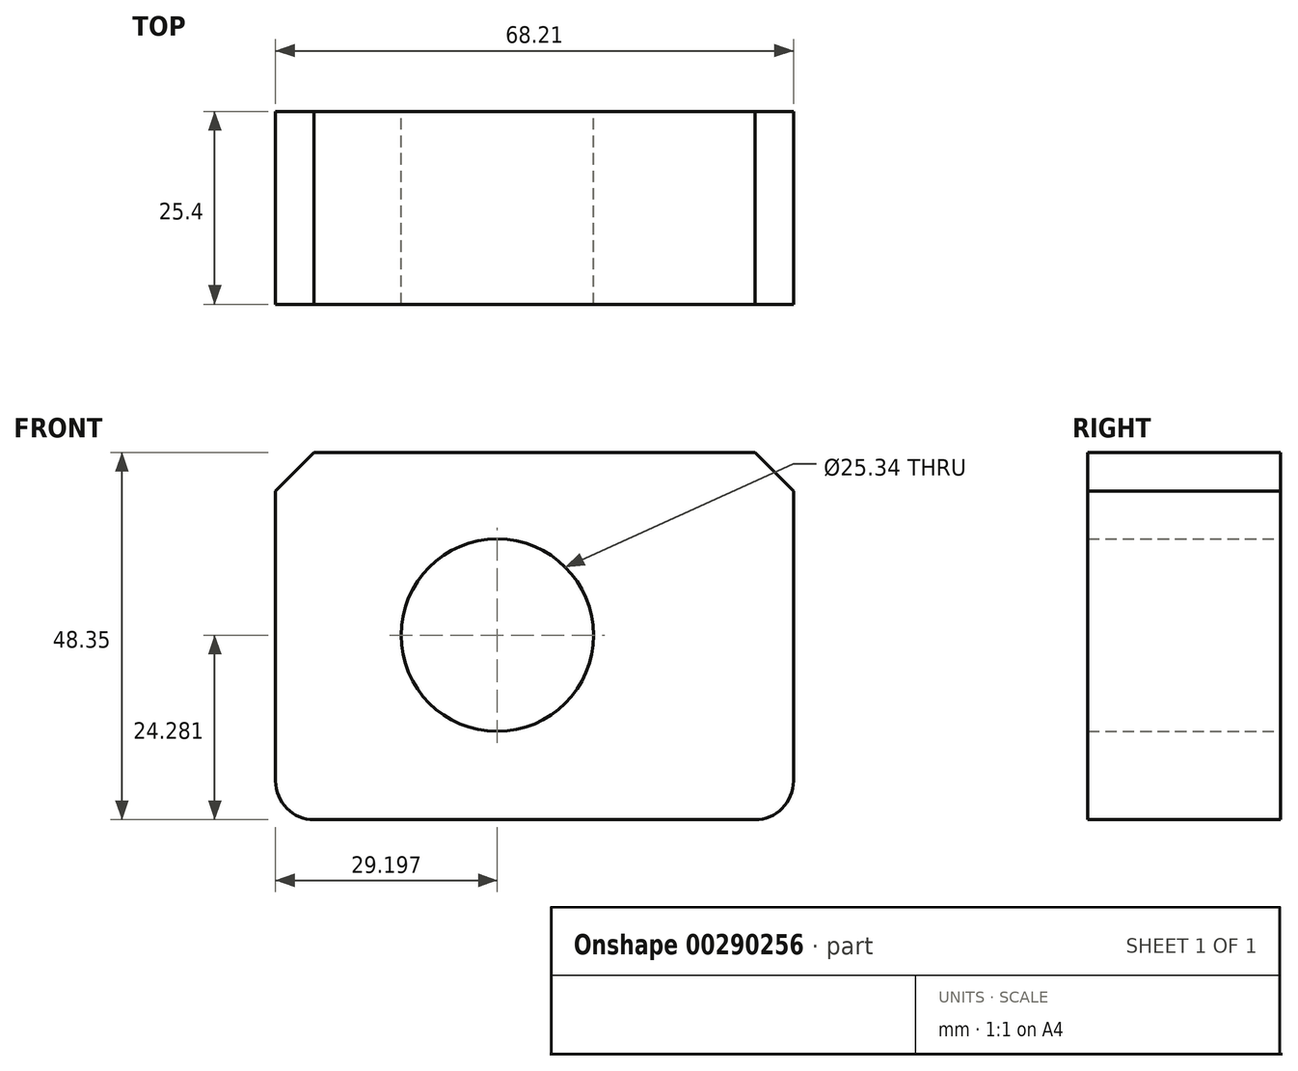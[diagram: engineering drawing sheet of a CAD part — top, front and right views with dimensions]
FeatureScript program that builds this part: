
annotation { "Feature Type Name" : "Feature", "Feature Type Description" : "" }
export const myFeature = defineFeature(function(context is Context, id is Id, definition is map)
    precondition{}
    {
        {
            var Q0;
            Q0=qCreatedBy(makeId("Front.planeOp"),FACE);
            var sketch = newSketch(context, id + "F0", { "sketchPlane" : qUnion([Q0])});
            skLineSegment(sketch, "E0.bottom", {"start": v(-45.19, 35.69) * mm, "end": v(23.02, 35.69) * mm});
            skLineSegment(sketch, "E0.top", {"start": v(-45.19, -12.66) * mm, "end": v(23.02, -12.66) * mm});
            skLineSegment(sketch, "E0.left", {"start": v(-45.19, 35.69) * mm, "end": v(-45.19, -12.66) * mm});
            skLineSegment(sketch, "E0.right", {"start": v(23.02, 35.69) * mm, "end": v(23.02, -12.66) * mm});
            skCircle(sketch, "E1", {"center": v(-16, 11.62) * mm, "radius": 12.67 * mm});
            skSolve(sketch);
        }
        {
            var Q0;
            Q0 = qSketchRegion(id + "F0", true);
            extrude(context, id + "F1", {"entities" : qUnion([Q0]), "depth" : 25.4 * mm});
        }
        {
            var Q0;
            Q0=makeQuery(id+"F1.opExtrude","SWEPT_EDGE",EDGE,{"disambiguationData":[OSD([sQuery(id+"F0.wireOp",EDGE,"E0.bottom"),sQuery(id+"F0.wireOp",EDGE,"E0.right")])]});
            var Q1;
            Q1=makeQuery(id+"F1.opExtrude","SWEPT_EDGE",EDGE,{"disambiguationData":[OSD([sQuery(id+"F0.wireOp",EDGE,"E0.bottom"),sQuery(id+"F0.wireOp",EDGE,"E0.left")])]});
            chamfer(context, id + "F2", {"entities" : qUnion([Q0, Q1]), "chamferType" : ChamferType.OFFSET_ANGLE, "width" : 5.08 * mm, "oppositeDirection" : false, "angle" : 45 * degree, "tangentPropagation" : true});
        }
        {
            var Q0;
            Q0=makeQuery(id+"F1.opExtrude","SWEPT_EDGE",EDGE,{"disambiguationData":[OSD([sQuery(id+"F0.wireOp",EDGE,"E0.top"),sQuery(id+"F0.wireOp",EDGE,"E0.left")])]});
            var Q1;
            Q1=makeQuery(id+"F1.opExtrude","SWEPT_EDGE",EDGE,{"disambiguationData":[OSD([sQuery(id+"F0.wireOp",EDGE,"E0.top"),sQuery(id+"F0.wireOp",EDGE,"E0.right")])]});
            fillet(context, id + "F3", {"entities" : qUnion([Q0, Q1]), "radius" : 5.08 * mm, "tangentPropagation" : true, "allowEdgeOverflow" : false});
        }
    });
